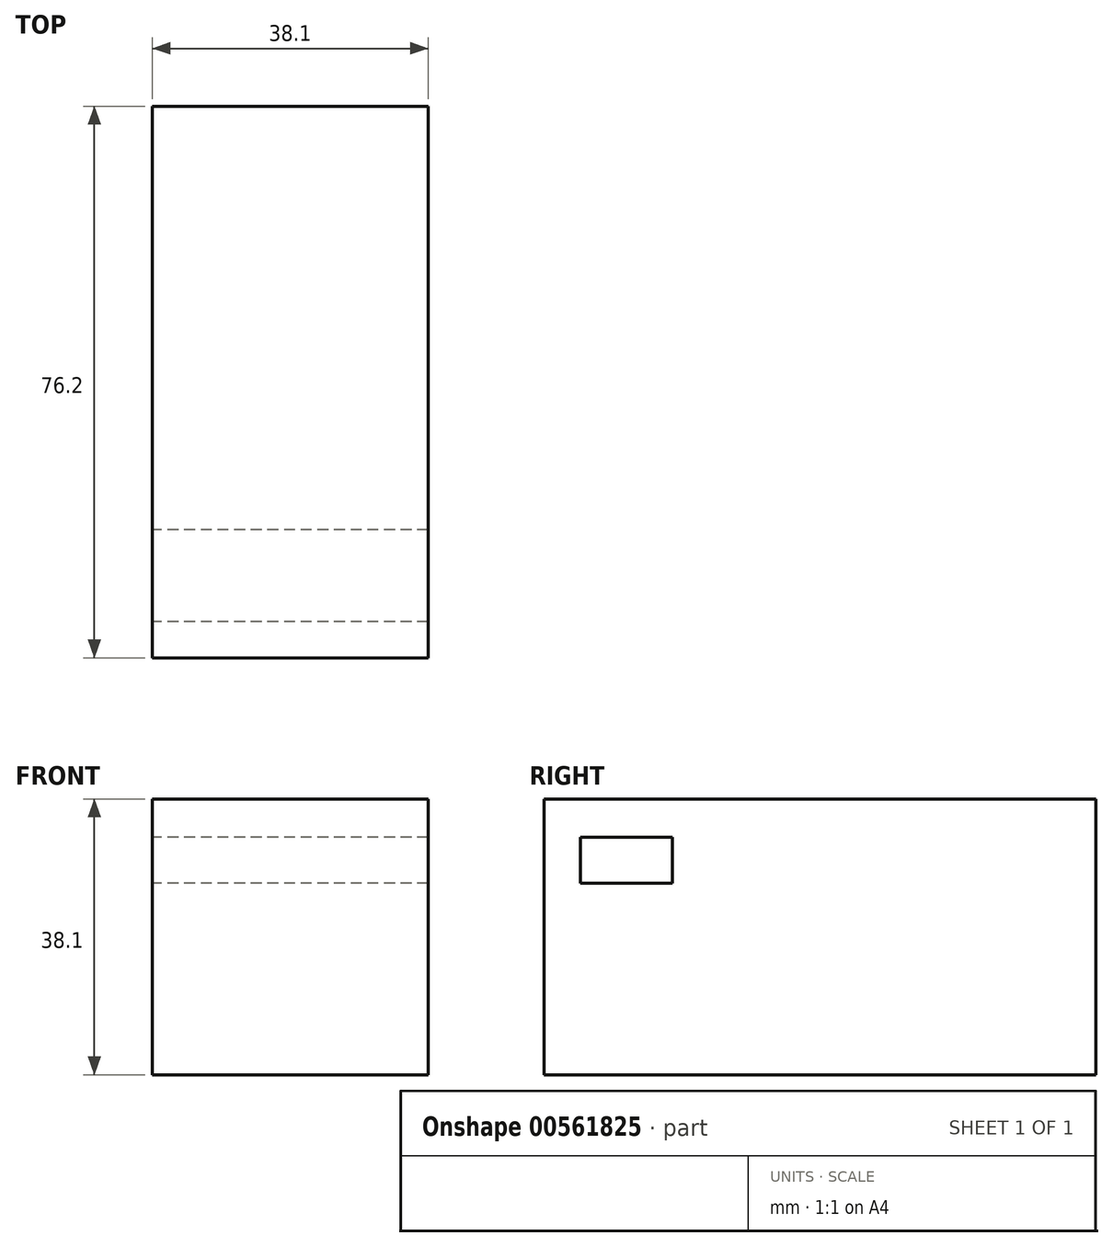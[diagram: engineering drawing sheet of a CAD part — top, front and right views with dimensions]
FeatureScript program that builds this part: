
annotation { "Feature Type Name" : "Feature", "Feature Type Description" : "" }
export const myFeature = defineFeature(function(context is Context, id is Id, definition is map)
    precondition{}
    {
        {
            var Q0;
            Q0=qCreatedBy(makeId("Front.planeOp"),FACE);
            var sketch = newSketch(context, id + "F0", { "sketchPlane" : qUnion([Q0])});
            skLineSegment(sketch, "E0.bottom", {"start": v(-19.05, 19.05) * mm, "end": v(19.05, 19.05) * mm});
            skLineSegment(sketch, "E0.top", {"start": v(-19.05, -19.05) * mm, "end": v(19.05, -19.05) * mm});
            skLineSegment(sketch, "E0.left", {"start": v(-19.05, 19.05) * mm, "end": v(-19.05, -19.05) * mm});
            skLineSegment(sketch, "E0.right", {"start": v(19.05, 19.05) * mm, "end": v(19.05, -19.05) * mm});
            skPoint(sketch, "E0.middle", {"position": v(0, 0) * mm});
            skSolve(sketch);
        }
        {
            var Q0;
            Q0 = qSketchRegion(id + "F0", true);
            extrude(context, id + "F1", {"entities" : qUnion([Q0]), "endBound" : BoundingType.SYMMETRIC, "depth" : 76.2 * mm, "offsetDistance" : 25.4 * mm});
        }
        {
            var Q0;
            Q0=makeQuery(id+"F1.opExtrude","SWEPT_FACE",FACE,{"disambiguationData":[OSD([sQuery(id+"F0.wireOp",EDGE,"E0.left")])]});
            var sketch = newSketch(context, id + "F2", { "sketchPlane" : qUnion([Q0])});
            skLineSegment(sketch, "E1.bottom", {"start": v(20.38, 13.75) * mm, "end": v(33.08, 13.75) * mm});
            skLineSegment(sketch, "E1.top", {"start": v(20.38, 7.4) * mm, "end": v(33.08, 7.4) * mm});
            skLineSegment(sketch, "E1.left", {"start": v(20.38, 13.75) * mm, "end": v(20.38, 7.4) * mm});
            skLineSegment(sketch, "E1.right", {"start": v(33.08, 13.75) * mm, "end": v(33.08, 7.4) * mm});
            skPoint(sketch, "E1.middle", {"position": v(26.73, 10.58) * mm});
            skSolve(sketch);
        }
        {
            var Q0;
            Q0 = qSketchRegion(id + "F2", true);
            extrude(context, id + "F3", {"entities" : qUnion([Q0]), "operationType" : NewBodyOperationType.REMOVE, "oppositeDirection" : true, "depth" : 38.1 * mm, "offsetDistance" : 25.4 * mm});
        }
    });
